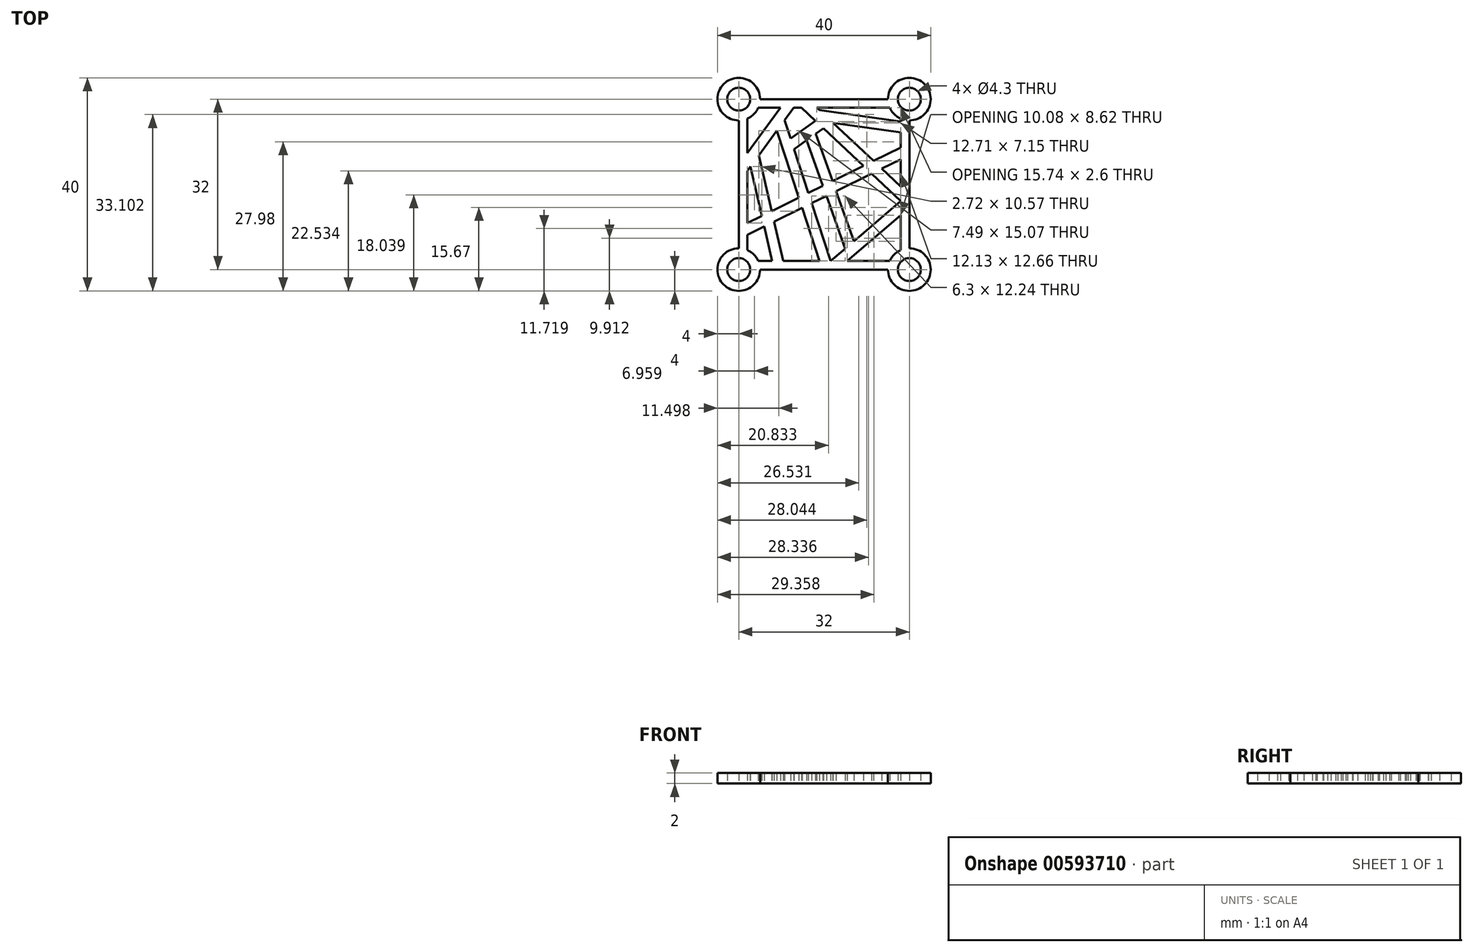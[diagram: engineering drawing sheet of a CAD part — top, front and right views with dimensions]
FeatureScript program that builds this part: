
annotation { "Feature Type Name" : "Feature", "Feature Type Description" : "" }
export const myFeature = defineFeature(function(context is Context, id is Id, definition is map)
    precondition{}
    {
        {
            var Q0;
            Q0=qCreatedBy(makeId("Top.planeOp"),FACE);
            var sketch = newSketch(context, id + "F0", { "sketchPlane" : qUnion([Q0])});
            skLineSegment(sketch, "E0.bottom", {"start": v(12, 16) * mm, "end": v(-12, 16) * mm});
            skLineSegment(sketch, "E0.top", {"start": v(12, -16) * mm, "end": v(-12, -16) * mm});
            skLineSegment(sketch, "E0.left", {"start": v(16, 12) * mm, "end": v(16, -12) * mm});
            skLineSegment(sketch, "E0.right", {"start": v(-16, 12) * mm, "end": v(-16, -12) * mm});
            skCircle(sketch, "E1", {"center": v(-16, 16) * mm, "radius": 2.15 * mm});
            skCircle(sketch, "E2", {"center": v(16, 16) * mm, "radius": 2.15 * mm});
            skCircle(sketch, "E3", {"center": v(-16, -16) * mm, "radius": 2.15 * mm});
            skCircle(sketch, "E4", {"center": v(16, -16) * mm, "radius": 2.15 * mm});
            skArc(sketch, "E5", {"start": v(-14.4, 12.33) * mm, "mid": v(-13.17, 13.17) * mm, "end": v(-12.33, 14.4) * mm});
            skArc(sketch, "E6", {"start": v(12.33, 14.4) * mm, "mid": v(13.17, 13.17) * mm, "end": v(14.4, 12.33) * mm});
            skArc(sketch, "E7", {"start": v(14.4, -12.33) * mm, "mid": v(13.17, -13.17) * mm, "end": v(12.33, -14.4) * mm});
            skArc(sketch, "E8", {"start": v(-12.33, -14.4) * mm, "mid": v(-13.17, -13.17) * mm, "end": v(-14.4, -12.33) * mm});
            skLineSegment(sketch, "E9.0", {"start": v(-14.4, 12.33) * mm, "end": v(-14.4, 5.9) * mm});
            skLineSegment(sketch, "E9.1", {"start": v(12.33, 14.4) * mm, "end": v(-1.34, 14.4) * mm});
            skLineSegment(sketch, "E9.2", {"start": v(14.4, 12.33) * mm, "end": v(14.4, 11.8) * mm});
            skLineSegment(sketch, "E9.3", {"start": v(12.33, -14.4) * mm, "end": v(4.32, -14.4) * mm});
            skArc(sketch, "E10.trimOffspring", {"start": v(-12, 16) * mm, "mid": v(-18.83, 18.83) * mm, "end": v(-16, 12) * mm});
            skArc(sketch, "E11.trimOffspring", {"start": v(16, 12) * mm, "mid": v(18.83, 18.83) * mm, "end": v(12, 16) * mm});
            skArc(sketch, "E12.trimOffspring", {"start": v(-16, -12) * mm, "mid": v(-18.83, -18.83) * mm, "end": v(-12, -16) * mm});
            skArc(sketch, "E13.trimOffspring", {"start": v(12, -16) * mm, "mid": v(18.83, -18.83) * mm, "end": v(16, -12) * mm});
            skLineSegment(sketch, "E14", {"start": v(-14.4, 5.9) * mm, "end": v(-8.19, 14.4) * mm});
            skLineSegment(sketch, "E15", {"start": v(-7.42, 12.06) * mm, "end": v(-6.3, 8.6) * mm});
            skLineSegment(sketch, "E16", {"start": v(1.24, -14.4) * mm, "end": v(3.98, -12.05) * mm});
            skLineSegment(sketch, "E17", {"start": v(14.4, -3.14) * mm, "end": v(8.93, 2) * mm});
            skLineSegment(sketch, "E18", {"start": v(-0.83, 13.92) * mm, "end": v(14.4, 11.8) * mm});
            skLineSegment(sketch, "E19", {"start": v(-13.8, 3.33) * mm, "end": v(-11.68, -5.91) * mm});
            skLineSegment(sketch, "E20.0", {"start": v(-12.25, 5.46) * mm, "end": v(-9.84, -5) * mm});
            skLineSegment(sketch, "E20.1", {"start": v(-14.4, 2.51) * mm, "end": v(-13.8, 3.33) * mm});
            skLineSegment(sketch, "E20.2", {"start": v(1.69, 11.55) * mm, "end": v(14.4, 9.79) * mm});
            skLineSegment(sketch, "E20.3", {"start": v(14.4, -0.4) * mm, "end": v(10.84, 2.94) * mm});
            skLineSegment(sketch, "E20.4", {"start": v(4.32, -14.4) * mm, "end": v(14.4, -5.78) * mm});
            skLineSegment(sketch, "E20.5", {"start": v(-8.87, 10.07) * mm, "end": v(-4.76, -2.5) * mm});
            skLineSegment(sketch, "E21.trimOffspring", {"start": v(14.4, -5.78) * mm, "end": v(14.4, -12.33) * mm});
            skLineSegment(sketch, "E22.trimOffspring", {"start": v(-0.86, -14.4) * mm, "end": v(-7.68, -14.4) * mm});
            skLineSegment(sketch, "E23.trimOffspring", {"start": v(14.4, 9.79) * mm, "end": v(14.4, 6.92) * mm});
            skLineSegment(sketch, "E24.trimOffspring", {"start": v(-9.73, -14.4) * mm, "end": v(-12.33, -14.4) * mm});
            skLineSegment(sketch, "E25", {"start": v(-14.4, -9.48) * mm, "end": v(-11.22, -7.91) * mm});
            skLineSegment(sketch, "E26.0", {"start": v(-14.4, -7.25) * mm, "end": v(-11.68, -5.91) * mm});
            skLineSegment(sketch, "E27.trimOffspring", {"start": v(-14.4, -9.48) * mm, "end": v(-14.4, -12.33) * mm});
            skLineSegment(sketch, "E28.trimOffspring", {"start": v(-11.22, -7.91) * mm, "end": v(-9.73, -14.4) * mm});
            skLineSegment(sketch, "E29.trimOffspring", {"start": v(-9.84, -5) * mm, "end": v(-4.76, -2.5) * mm});
            skLineSegment(sketch, "E30.trimOffspring", {"start": v(-9.38, -7) * mm, "end": v(-7.68, -14.4) * mm});
            skLineSegment(sketch, "E31.trimOffspring", {"start": v(-9.38, -7) * mm, "end": v(-4.13, -4.42) * mm});
            skLineSegment(sketch, "E32.trimOffspring", {"start": v(-4.13, -4.42) * mm, "end": v(-0.86, -14.4) * mm});
            skLineSegment(sketch, "E33.trimOffspring", {"start": v(-2.95, -1.61) * mm, "end": v(-0.2, -0.27) * mm});
            skLineSegment(sketch, "E34.trimOffspring", {"start": v(-2.32, -3.53) * mm, "end": v(0.47, -2.16) * mm});
            skLineSegment(sketch, "E35.trimOffspring", {"start": v(-2.32, -3.53) * mm, "end": v(1.24, -14.4) * mm});
            skLineSegment(sketch, "E36.trimOffspring", {"start": v(9.29, 4.4) * mm, "end": v(14.4, 6.92) * mm});
            skLineSegment(sketch, "E37.trimOffspring", {"start": v(7.37, 3.46) * mm, "end": v(-0.13, 10.52) * mm});
            skLineSegment(sketch, "E38.trimOffspring", {"start": v(10.84, 2.94) * mm, "end": v(14.4, 4.7) * mm});
            skLineSegment(sketch, "E39.trimOffspring", {"start": v(9.29, 4.4) * mm, "end": v(1.69, 11.55) * mm});
            skLineSegment(sketch, "E40", {"start": v(-1.62, 11.92) * mm, "end": v(-6.3, 8.6) * mm});
            skLineSegment(sketch, "E41", {"start": v(3.98, -12.05) * mm, "end": v(0.47, -2.16) * mm});
            skLineSegment(sketch, "E42.0", {"start": v(-0.13, 10.52) * mm, "end": v(-1.56, 9.5) * mm});
            skLineSegment(sketch, "E43.0", {"start": v(5.61, -10.66) * mm, "end": v(2.27, -1.27) * mm});
            skLineSegment(sketch, "E44.trimOffspring", {"start": v(-1.62, 11.92) * mm, "end": v(-4.26, 14.4) * mm});
            skLineSegment(sketch, "E45.trimOffspring", {"start": v(-5.64, 6.62) * mm, "end": v(-2.95, -1.61) * mm});
            skLineSegment(sketch, "E46.trimOffspring", {"start": v(-3.26, 8.3) * mm, "end": v(-5.64, 6.62) * mm});
            skLineSegment(sketch, "E47.trimOffspring", {"start": v(1.6, 0.62) * mm, "end": v(7.37, 3.46) * mm});
            skLineSegment(sketch, "E48.trimOffspring", {"start": v(-0.2, -0.27) * mm, "end": v(-3.26, 8.3) * mm});
            skLineSegment(sketch, "E49.trimOffspring", {"start": v(1.6, 0.62) * mm, "end": v(-1.56, 9.5) * mm});
            skLineSegment(sketch, "E50.trimOffspring", {"start": v(5.61, -10.66) * mm, "end": v(14.4, -3.14) * mm});
            skLineSegment(sketch, "E51.trimOffspring", {"start": v(2.27, -1.27) * mm, "end": v(8.93, 2) * mm});
            skLineSegment(sketch, "E52.trimOffspring", {"start": v(-8.19, 14.4) * mm, "end": v(-12.33, 14.4) * mm});
            skLineSegment(sketch, "E53.trimOffspring", {"start": v(-4.26, 14.4) * mm, "end": v(-5.7, 14.4) * mm});
            skLineSegment(sketch, "E54.trimOffspring", {"start": v(-0.83, 13.92) * mm, "end": v(-1.34, 14.4) * mm});
            skLineSegment(sketch, "E55.trimOffspring", {"start": v(-7.42, 12.06) * mm, "end": v(-5.7, 14.4) * mm});
            skLineSegment(sketch, "E56.trimOffspring", {"start": v(14.4, 4.7) * mm, "end": v(14.4, -0.4) * mm});
            skLineSegment(sketch, "E57.trimOffspring", {"start": v(-12.25, 5.46) * mm, "end": v(-8.87, 10.07) * mm});
            skLineSegment(sketch, "E58.trimOffspring", {"start": v(-14.4, 2.51) * mm, "end": v(-14.4, -7.25) * mm});
            skSolve(sketch);
        }
        {
            var Q0;
            Q0=makeQuery(id+"F0.imprint","IMPRINT",FACE,{"disambiguationData":[TD([[makeQuery(id+"F0.imprint","IMPRINT",EDGE,{"derivedFrom":sQuery(id+"F0.wireOp",EDGE,"E0.bottom")}),1.0]])]});
            extrude(context, id + "F1", {"entities" : qUnion([Q0]), "depth" : 2 * mm, "offsetDistance" : 25 * mm});
        }
    });
